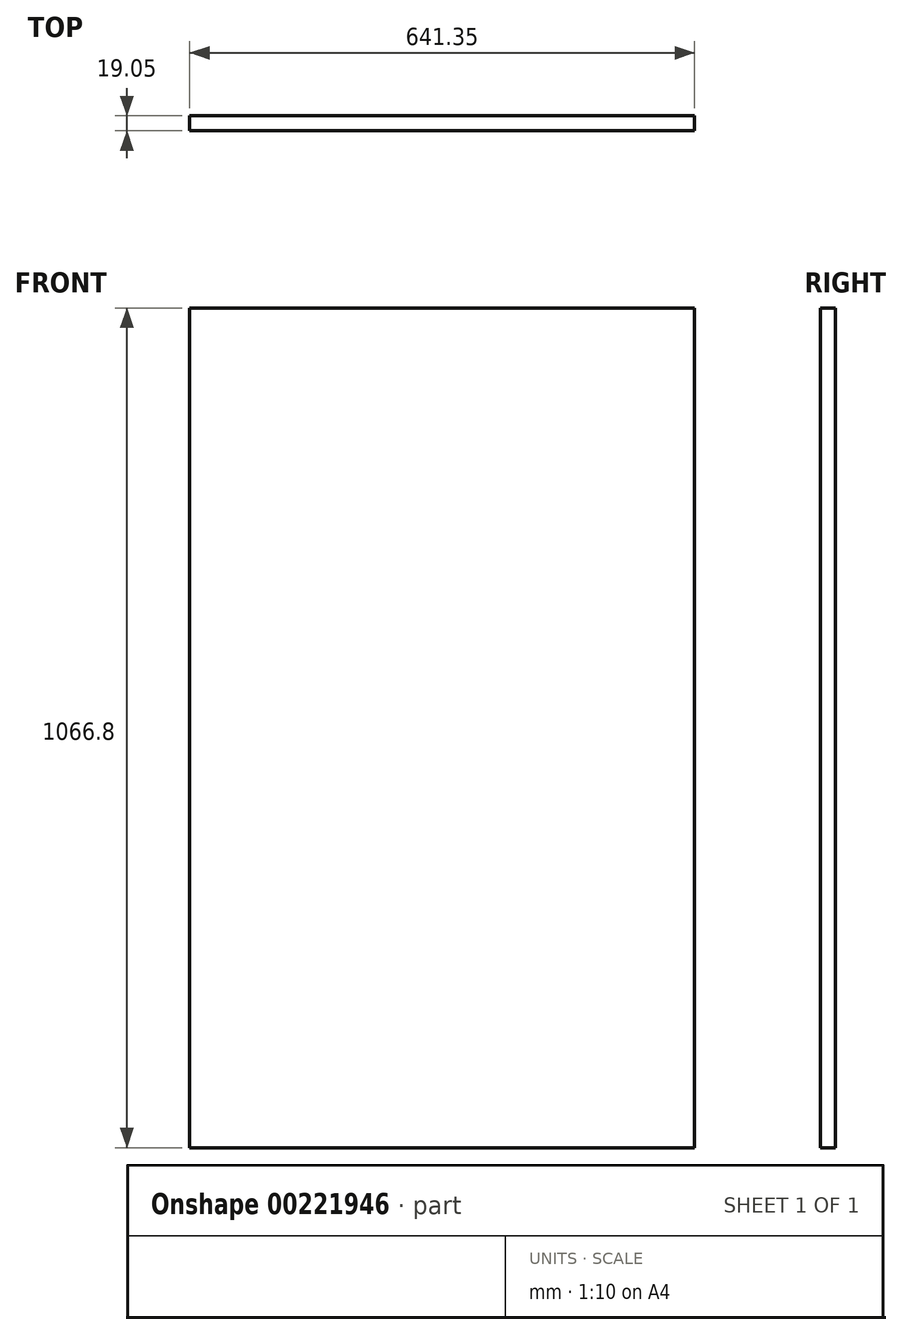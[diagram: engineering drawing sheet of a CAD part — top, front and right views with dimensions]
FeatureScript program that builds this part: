
annotation { "Feature Type Name" : "Feature", "Feature Type Description" : "" }
export const myFeature = defineFeature(function(context is Context, id is Id, definition is map)
    precondition{}
    {
        {
            var Q0;
            Q0=qCreatedBy(makeId("Front.planeOp"),FACE);
            var sketch = newSketch(context, id + "F0", { "sketchPlane" : qUnion([Q0])});
            skLineSegment(sketch, "E0.bottom", {"start": v(-343.4, 793.4) * mm, "end": v(297.95, 793.4) * mm});
            skLineSegment(sketch, "E0.top", {"start": v(-343.4, -273.4) * mm, "end": v(297.95, -273.4) * mm});
            skLineSegment(sketch, "E0.left", {"start": v(-343.4, 793.4) * mm, "end": v(-343.4, -273.4) * mm});
            skLineSegment(sketch, "E0.right", {"start": v(297.95, 793.4) * mm, "end": v(297.95, -273.4) * mm});
            skSolve(sketch);
        }
        {
            var Q0;
            Q0 = qSketchRegion(id + "F0", true);
            extrude(context, id + "F1", {"entities" : qUnion([Q0]), "depth" : 19.05 * mm});
        }
    });
